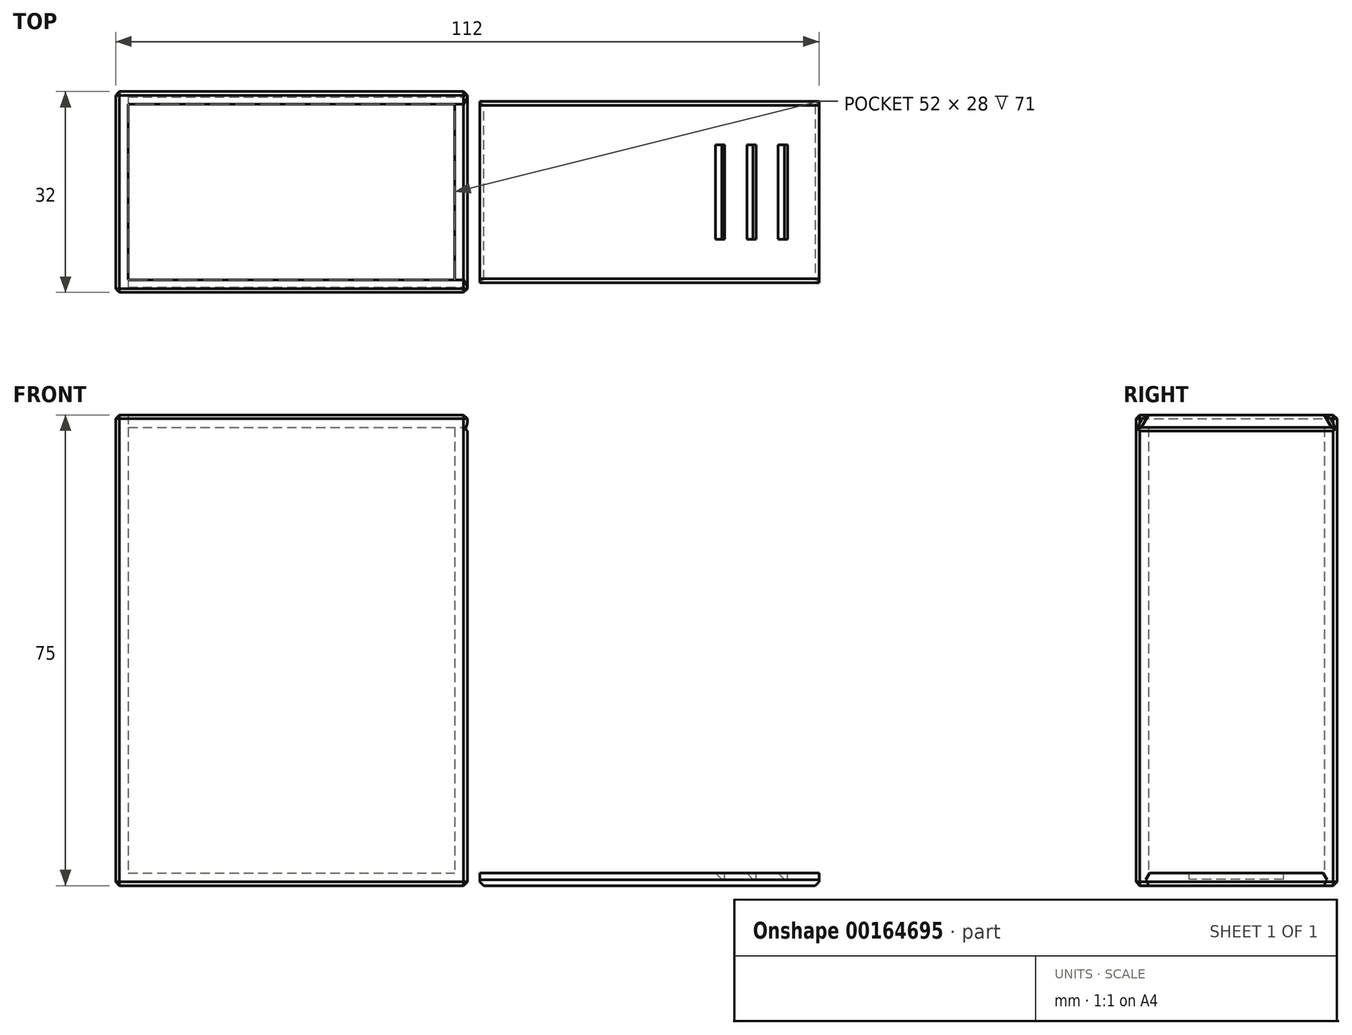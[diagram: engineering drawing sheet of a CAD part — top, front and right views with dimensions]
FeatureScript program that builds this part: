
annotation { "Feature Type Name" : "Feature", "Feature Type Description" : "" }
export const myFeature = defineFeature(function(context is Context, id is Id, definition is map)
    precondition{}
    {
        {
            assignVariable(context, id + "F0", {"name" : "Height", "anyValue" : 75});
        }
        {
            assignVariable(context, id + "F1", {"name" : "Length", "anyValue" : 56});
        }
        {
            assignVariable(context, id + "F2", {"name" : "WallThickness", "anyValue" : 2});
        }
        {
            var Q0;
            Q0=qCreatedBy(makeId("Top.planeOp"),FACE);
            var sketch = newSketch(context, id + "F3", { "sketchPlane" : qUnion([Q0])});
            skLineSegment(sketch, "E0", {"start": v(0, 0) * mm, "end": v(56, 0) * mm});
            skLineSegment(sketch, "E1", {"start": v(56, 0) * mm, "end": v(56, 32) * mm});
            skLineSegment(sketch, "E2", {"start": v(56, 32) * mm, "end": v(0, 32) * mm});
            skLineSegment(sketch, "E3", {"start": v(0, 32) * mm, "end": v(0, 0) * mm});
            skLineSegment(sketch, "E4.0", {"start": v(2, 2) * mm, "end": v(54, 2) * mm});
            skLineSegment(sketch, "E4.1", {"start": v(2, 30) * mm, "end": v(2, 2) * mm});
            skLineSegment(sketch, "E4.2", {"start": v(54, 30) * mm, "end": v(2, 30) * mm});
            skLineSegment(sketch, "E4.3", {"start": v(54, 2) * mm, "end": v(54, 30) * mm});
            skLineSegment(sketch, "E5", {"start": v(54, 2) * mm, "end": v(56, 2) * mm});
            skLineSegment(sketch, "E6", {"start": v(54, 30) * mm, "end": v(56, 30) * mm});
            skLineSegment(sketch, "E7", {"start": v(28, 32) * mm, "end": v(28, 0) * mm, "construction": true});
            skLineSegment(sketch, "E8", {"start": v(29, 2) * mm, "end": v(29, 30) * mm});
            skLineSegment(sketch, "E9.MirrorCS", {"start": v(27, 2) * mm, "end": v(27, 30) * mm});
            skSolve(sketch);
        }
        {
            var Q0;
            Q0=makeQuery(id+"F3.imprint","IMPRINT",FACE,{"disambiguationData":[TD([[makeQuery(id+"F3.imprint","IMPRINT",EDGE,{"derivedFrom":sQuery(id+"F3.wireOp",EDGE,"E0")}),1.0]])]});
            extrude(context, id + "F4", {"entities" : qUnion([Q0]), "depth" : (getVariable(context, 'Height')) * mm});
        }
        {
            var Q0;
            Q0=makeQuery(id+"F3.imprint","IMPRINT",FACE,{"disambiguationData":[TD([[makeQuery(id+"F3.imprint","IMPRINT",EDGE,{"derivedFrom":sQuery(id+"F3.wireOp",EDGE,"E4.0")}),1.0]])]});
            extrude(context, id + "F5", {"entities" : qUnion([Q0]), "operationType" : NewBodyOperationType.ADD, "depth" : (getVariable(context, 'WallThickness')) * mm});
        }
        {
            var Q0;
            Q0=makeQuery(id+"F3.imprint","IMPRINT",FACE,{"disambiguationData":[TD([[makeQuery(id+"F3.imprint","IMPRINT",EDGE,{"derivedFrom":sQuery(id+"F3.wireOp",EDGE,"E4.3")}),-1.0]])]});
            extrude(context, id + "F6", {"entities" : qUnion([Q0]), "operationType" : NewBodyOperationType.ADD, "depth" : (getVariable(context, 'Height') - getVariable(context, 'WallThickness')) * mm});
        }
        {
            var Q0;
            {var subQ0=sQuery(id+"F3.wireOp",EDGE,"E1");Q0=makeQuery(id+"F6.boolean.opBoolean","MERGE",FACE,{"derivedFrom":[makeQuery(id+"F4.opExtrude","SWEPT_FACE",FACE,{"disambiguationData":[OSD([subQ0]),TDD([makeQuery(id+"F3.imprint","IMPRINT",EDGE,{"disambiguationData":[TD([[makeQuery(id+"F3.imprint","INTERSECT",VERTEX,{"derivedFrom":[sQuery(id+"F3.wireOp",EDGE,"E0"),subQ0]}),-1.0]])],"derivedFrom":subQ0})])]}),makeQuery(id+"F4.opExtrude","SWEPT_FACE",FACE,{"disambiguationData":[OSD([subQ0]),TDD([makeQuery(id+"F3.imprint","IMPRINT",EDGE,{"disambiguationData":[TD([[makeQuery(id+"F3.imprint","INTERSECT",VERTEX,{"derivedFrom":[subQ0,sQuery(id+"F3.wireOp",EDGE,"E2")]}),1.0]])],"derivedFrom":subQ0})])]}),makeQuery(id+"F6.opExtrude","SWEPT_FACE",FACE,{"disambiguationData":[OSD([subQ0])]})]});}
            var sketch = newSketch(context, id + "F7", { "sketchPlane" : qUnion([Q0])});
            skLineSegment(sketch, "E10.0", {"start": v(2, 73) * mm, "end": v(30, 73) * mm});
            skLineSegment(sketch, "E10.1", {"start": v(0, 75) * mm, "end": v(2, 75) * mm, "construction": true});
            skLineSegment(sketch, "E10.2", {"start": v(30, 75) * mm, "end": v(32, 75) * mm, "construction": true});
            skLineSegment(sketch, "E10.3", {"start": v(32, 75) * mm, "end": v(32, 0) * mm, "construction": true});
            skLineSegment(sketch, "E10.4", {"start": v(0, 75) * mm, "end": v(0, 0) * mm, "construction": true});
            skLineSegment(sketch, "E11", {"start": v(2, 75) * mm, "end": v(0.85, 73) * mm});
            skLineSegment(sketch, "E12", {"start": v(0.85, 73) * mm, "end": v(2, 73) * mm});
            skPoint(sketch, "E13", {"position": v(16, 73) * mm});
            skLineSegment(sketch, "E14", {"start": v(16, 104.43) * mm, "end": v(16, 92.5) * mm, "construction": true});
            skLineSegment(sketch, "E15.MirrorCS", {"start": v(30, 75) * mm, "end": v(31.15, 73) * mm});
            skLineSegment(sketch, "E16.MirrorCS", {"start": v(31.15, 73) * mm, "end": v(30, 73) * mm});
            skLineSegment(sketch, "E17", {"start": v(2, 75) * mm, "end": v(30, 75) * mm});
            skLineSegment(sketch, "E18", {"start": v(1.05, 73) * mm, "end": v(2.2, 75) * mm});
            skLineSegment(sketch, "E19.MirrorCS", {"start": v(30.95, 73) * mm, "end": v(29.8, 75) * mm});
            skSolve(sketch);
        }
        {
            var Q0;
            Q0=makeQuery(id+"F7.imprint","IMPRINT",FACE,{"disambiguationData":[TD([[makeQuery(id+"F7.imprint","IMPRINT",EDGE,{"derivedFrom":sQuery(id+"F7.wireOp",EDGE,"E11")}),1.0]])]});
            var Q1;
            Q1=makeQuery(id+"F7.imprint","IMPRINT",FACE,{"disambiguationData":[TD([[makeQuery(id+"F7.imprint","IMPRINT",EDGE,{"derivedFrom":sQuery(id+"F7.wireOp",EDGE,"E15.MirrorCS")}),-1.0]])]});
            var Q2;
            {var subQ0=sQuery(id+"F7.wireOp",EDGE,"E12");var subQ3=sQuery(id+"F7.wireOp",EDGE,"E18");var subQ4=makeQuery(id+"F7.imprint","INTERSECT",VERTEX,{"derivedFrom":[subQ0,subQ3]});Q2=makeQuery(id+"F7.imprint","IMPRINT",FACE,{"disambiguationData":[TD([[makeQuery(id+"F7.imprint","IMPRINT",EDGE,{"disambiguationData":[TD([[subQ4,-1.0]])],"derivedFrom":subQ3}),-1.0]])]});}
            var Q3;
            {var subQ0=sQuery(id+"F7.wireOp",EDGE,"E16.MirrorCS");var subQ3=sQuery(id+"F7.wireOp",EDGE,"E19.MirrorCS");var subQ4=makeQuery(id+"F7.imprint","INTERSECT",VERTEX,{"derivedFrom":[subQ0,subQ3]});Q3=makeQuery(id+"F7.imprint","IMPRINT",FACE,{"disambiguationData":[TD([[makeQuery(id+"F7.imprint","IMPRINT",EDGE,{"disambiguationData":[TD([[subQ4,-1.0]])],"derivedFrom":subQ3}),1.0]])]});}
            extrude(context, id + "F8", {"entities" : qUnion([Q0, Q1, Q2, Q3]), "operationType" : NewBodyOperationType.REMOVE, "oppositeDirection" : true, "depth" : (getVariable(context, 'Length') - getVariable(context, 'WallThickness')) * mm});
        }
        {
            var Q0;
            Q0=makeQuery(id+"F7.imprint","IMPRINT",FACE,{"disambiguationData":[TD([[makeQuery(id+"F7.imprint","IMPRINT",EDGE,{"derivedFrom":sQuery(id+"F7.wireOp",EDGE,"E10.0")}),1.0]])]});
            var Q1;
            {var subQ0=sQuery(id+"F7.wireOp",EDGE,"E12");var subQ3=sQuery(id+"F7.wireOp",EDGE,"E18");var subQ4=makeQuery(id+"F7.imprint","INTERSECT",VERTEX,{"derivedFrom":[subQ0,subQ3]});Q1=makeQuery(id+"F7.imprint","IMPRINT",FACE,{"disambiguationData":[TD([[makeQuery(id+"F7.imprint","IMPRINT",EDGE,{"disambiguationData":[TD([[subQ4,-1.0]])],"derivedFrom":subQ3}),-1.0]])]});}
            var Q2;
            {var subQ0=sQuery(id+"F7.wireOp",EDGE,"E16.MirrorCS");var subQ3=sQuery(id+"F7.wireOp",EDGE,"E19.MirrorCS");var subQ4=makeQuery(id+"F7.imprint","INTERSECT",VERTEX,{"derivedFrom":[subQ0,subQ3]});Q2=makeQuery(id+"F7.imprint","IMPRINT",FACE,{"disambiguationData":[TD([[makeQuery(id+"F7.imprint","IMPRINT",EDGE,{"disambiguationData":[TD([[subQ4,-1.0]])],"derivedFrom":subQ3}),1.0]])]});}
            extrude(context, id + "F9", {"entities" : qUnion([Q0, Q1, Q2]), "depth" : (getVariable(context, 'Length')) * mm, "hasSecondDirection" : true, "secondDirectionOppositeDirection" : false, "secondDirectionDepth" : (getVariable(context, 'WallThickness')) * mm});
        }
        {
            var Q0;
            Q0=makeQuery(id+"F9.opExtrude","SWEPT_BODY",BODY,{"disambiguationData":[OSD([sQuery(id+"F7.wireOp",EDGE,"E10.0"),sQuery(id+"F7.wireOp",EDGE,"E12"),sQuery(id+"F7.wireOp",EDGE,"E16.MirrorCS"),sQuery(id+"F7.wireOp",EDGE,"E17"),sQuery(id+"F7.wireOp",EDGE,"E18"),sQuery(id+"F7.wireOp",EDGE,"E19.MirrorCS")])]});
            transform(context, id + "F10", {"entities" : qUnion([Q0]), "transformType" : TransformType.TRANSLATION_3D, "dx" : 0 * mm, "dy" : 0 * mm, "dz" : (-getVariable(context, 'Height') + getVariable(context, 'WallThickness')) * mm, "makeCopy" : false});
        }
        {
            var Q0;
            Q0=makeQuery(id+"F9.opExtrude","SWEPT_FACE",FACE,{"disambiguationData":[OSD([sQuery(id+"F7.wireOp",EDGE,"E17")])]});
            var sketch = newSketch(context, id + "F11", { "sketchPlane" : qUnion([Q0])});
            skLineSegment(sketch, "E20.0", {"start": v(112, 2.2) * mm, "end": v(112, 29.8) * mm, "construction": true});
            skLineSegment(sketch, "E20.1", {"start": v(112, 29.8) * mm, "end": v(58, 29.8) * mm, "construction": true});
            skLineSegment(sketch, "E20.2", {"start": v(112, 2.2) * mm, "end": v(58, 2.2) * mm, "construction": true});
            skLineSegment(sketch, "E20.3", {"start": v(58, 2.2) * mm, "end": v(58, 29.8) * mm, "construction": true});
            skLineSegment(sketch, "E21", {"start": v(107, 23.5) * mm, "end": v(107, 8.5) * mm});
            skLineSegment(sketch, "E22", {"start": v(107, 8.5) * mm, "end": v(104, 8.5) * mm});
            skLineSegment(sketch, "E23", {"start": v(104, 8.5) * mm, "end": v(104, 23.5) * mm});
            skLineSegment(sketch, "E24", {"start": v(104, 23.5) * mm, "end": v(107, 23.5) * mm});
            skPoint(sketch, "E25", {"position": v(107, 16) * mm});
            skPoint(sketch, "E26", {"position": v(112, 16) * mm});
            skLineSegment(sketch, "E27.1.0.0", {"start": v(102, 23.5) * mm, "end": v(102, 8.5) * mm});
            skLineSegment(sketch, "E27.1.0.1", {"start": v(102, 8.5) * mm, "end": v(99, 8.5) * mm});
            skLineSegment(sketch, "E27.1.0.2", {"start": v(99, 8.5) * mm, "end": v(99, 23.5) * mm});
            skLineSegment(sketch, "E27.1.0.3", {"start": v(99, 23.5) * mm, "end": v(102, 23.5) * mm});
            skLineSegment(sketch, "E27.2.0.0", {"start": v(97, 23.5) * mm, "end": v(97, 8.5) * mm});
            skLineSegment(sketch, "E27.2.0.1", {"start": v(97, 8.5) * mm, "end": v(94, 8.5) * mm});
            skLineSegment(sketch, "E27.2.0.2", {"start": v(94, 8.5) * mm, "end": v(94, 23.5) * mm});
            skLineSegment(sketch, "E27.2.0.3", {"start": v(94, 23.5) * mm, "end": v(97, 23.5) * mm});
            skLineSegment(sketch, "E27.direction1", {"start": v(104, 8.5) * mm, "end": v(99, 8.5) * mm, "construction": true});
            skSolve(sketch);
        }
        {
            var Q0;
            Q0=makeQuery(id+"F11.imprint","IMPRINT",FACE,{"disambiguationData":[TD([[makeQuery(id+"F11.imprint","IMPRINT",EDGE,{"derivedFrom":sQuery(id+"F11.wireOp",EDGE,"E27.2.0.0")}),-1.0]])]});
            var Q1;
            Q1=makeQuery(id+"F11.imprint","IMPRINT",FACE,{"disambiguationData":[TD([[makeQuery(id+"F11.imprint","IMPRINT",EDGE,{"derivedFrom":sQuery(id+"F11.wireOp",EDGE,"E27.1.0.0")}),-1.0]])]});
            var Q2;
            Q2=makeQuery(id+"F11.imprint","IMPRINT",FACE,{"disambiguationData":[TD([[makeQuery(id+"F11.imprint","IMPRINT",EDGE,{"derivedFrom":sQuery(id+"F11.wireOp",EDGE,"E21")}),-1.0]])]});
            extrude(context, id + "F12", {"entities" : qUnion([Q0, Q1, Q2]), "operationType" : NewBodyOperationType.REMOVE, "oppositeDirection" : true, "depth" : (getVariable(context, 'WallThickness') / 2) * mm});
        }
        {
            var Q0;
            Q0=makeQuery(id+"F12.boolean.opBoolean","COPY",EDGE,{"derivedFrom":makeQuery(id+"F12.opExtrude","CAP_EDGE",EDGE,{"disambiguationData":[OSD([sQuery(id+"F11.wireOp",EDGE,"E23")])],"isStart":false})});
            var Q1;
            Q1=makeQuery(id+"F12.boolean.opBoolean","COPY",EDGE,{"derivedFrom":makeQuery(id+"F12.opExtrude","CAP_EDGE",EDGE,{"disambiguationData":[OSD([sQuery(id+"F11.wireOp",EDGE,"E27.1.0.2")])],"isStart":false})});
            var Q2;
            Q2=makeQuery(id+"F12.boolean.opBoolean","COPY",EDGE,{"derivedFrom":makeQuery(id+"F12.opExtrude","CAP_EDGE",EDGE,{"disambiguationData":[OSD([sQuery(id+"F11.wireOp",EDGE,"E27.2.0.2")])],"isStart":false})});
            chamfer(context, id + "F13", {"entities" : qUnion([Q0, Q1, Q2]), "width" : 2.5 * mm, "tangentPropagation" : true});
        }
        {
            var Q0;
            Q0=makeQuery(id+"F4.opExtrude","SWEPT_FACE",FACE,{"disambiguationData":[OSD([sQuery(id+"F3.wireOp",EDGE,"E0")])]});
            var sketch = newSketch(context, id + "F14", { "sketchPlane" : qUnion([Q0])});
            skLineSegment(sketch, "E28.0", {"start": v(0, 75) * mm, "end": v(0, 0) * mm, "construction": true});
            skLineSegment(sketch, "E28.1", {"start": v(0, 75) * mm, "end": v(56, 75) * mm, "construction": true});
            skLineSegment(sketch, "E28.2", {"start": v(56, 75) * mm, "end": v(56, 0) * mm, "construction": true});
            skLineSegment(sketch, "E28.3", {"start": v(0, 0) * mm, "end": v(56, 0) * mm, "construction": true});
            skLineSegment(sketch, "E29", {"start": v(0, 37.5) * mm, "end": v(56, 37.5) * mm, "construction": true});
            skLineSegment(sketch, "E30", {"start": v(28, 75) * mm, "end": v(28, 0) * mm, "construction": true});
            skLineSegment(sketch, "E31", {"start": v(28, 55.5) * mm, "end": v(22, 55.5) * mm});
            skLineSegment(sketch, "E32", {"start": v(22, 55.5) * mm, "end": v(22, 43.5) * mm});
            skLineSegment(sketch, "E33", {"start": v(22, 43.5) * mm, "end": v(10, 43.5) * mm});
            skLineSegment(sketch, "E34", {"start": v(10, 43.5) * mm, "end": v(10, 37.5) * mm});
            skLineSegment(sketch, "E35.MirrorCS", {"start": v(28, 55.5) * mm, "end": v(34, 55.5) * mm});
            skLineSegment(sketch, "E36.MirrorCS", {"start": v(34, 55.5) * mm, "end": v(34, 43.5) * mm});
            skLineSegment(sketch, "E37.MirrorCS", {"start": v(46, 43.5) * mm, "end": v(46, 37.5) * mm});
            skLineSegment(sketch, "E38.MirrorCS", {"start": v(34, 43.5) * mm, "end": v(46, 43.5) * mm});
            skLineSegment(sketch, "E39.MirrorCS", {"start": v(10, 31.5) * mm, "end": v(10, 37.5) * mm});
            skLineSegment(sketch, "E40.MirrorCS", {"start": v(22, 31.5) * mm, "end": v(10, 31.5) * mm});
            skLineSegment(sketch, "E41.MirrorCS", {"start": v(22, 19.5) * mm, "end": v(22, 31.5) * mm});
            skLineSegment(sketch, "E42.MirrorCS", {"start": v(28, 19.5) * mm, "end": v(22, 19.5) * mm});
            skLineSegment(sketch, "E43.MirrorCS", {"start": v(28, 19.5) * mm, "end": v(34, 19.5) * mm});
            skLineSegment(sketch, "E44.MirrorCS", {"start": v(34, 19.5) * mm, "end": v(34, 31.5) * mm});
            skLineSegment(sketch, "E45.MirrorCS", {"start": v(46, 31.5) * mm, "end": v(46, 37.5) * mm});
            skLineSegment(sketch, "E46.MirrorCS", {"start": v(34, 31.5) * mm, "end": v(46, 31.5) * mm});
            skSolve(sketch);
        }
        {
            var Q0;
            Q0=makeQuery(id+"F4.opExtrude","SWEPT_FACE",FACE,{"disambiguationData":[OSD([sQuery(id+"F3.wireOp",EDGE,"E0")])]});
            var Q1;
            {var subQ0=sQuery(id+"F3.wireOp",EDGE,"E1");Q1=makeQuery(id+"F6.boolean.opBoolean","MERGE",FACE,{"derivedFrom":[makeQuery(id+"F4.opExtrude","SWEPT_FACE",FACE,{"disambiguationData":[OSD([subQ0]),TDD([makeQuery(id+"F3.imprint","IMPRINT",EDGE,{"disambiguationData":[TD([[makeQuery(id+"F3.imprint","INTERSECT",VERTEX,{"derivedFrom":[sQuery(id+"F3.wireOp",EDGE,"E0"),subQ0]}),-1.0]])],"derivedFrom":subQ0})])]}),makeQuery(id+"F4.opExtrude","SWEPT_FACE",FACE,{"disambiguationData":[OSD([subQ0]),TDD([makeQuery(id+"F3.imprint","IMPRINT",EDGE,{"disambiguationData":[TD([[makeQuery(id+"F3.imprint","INTERSECT",VERTEX,{"derivedFrom":[subQ0,sQuery(id+"F3.wireOp",EDGE,"E2")]}),1.0]])],"derivedFrom":subQ0})])]}),makeQuery(id+"F6.opExtrude","SWEPT_FACE",FACE,{"disambiguationData":[OSD([subQ0])]})]});}
            var Q2;
            Q2=makeQuery(id+"F4.opExtrude","SWEPT_FACE",FACE,{"disambiguationData":[OSD([sQuery(id+"F3.wireOp",EDGE,"E2")])]});
            var Q3;
            Q3=makeQuery(id+"F4.opExtrude","SWEPT_FACE",FACE,{"disambiguationData":[OSD([sQuery(id+"F3.wireOp",EDGE,"E3")])]});
            var Q4;
            {var subQ0=sQuery(id+"F3.wireOp",EDGE,"E6");var subQ1=sQuery(id+"F3.wireOp",EDGE,"E5");var subQ2=sQuery(id+"F3.wireOp",EDGE,"E4.3");var subQ3=sQuery(id+"F3.wireOp",EDGE,"E1");var subQ4=sQuery(id+"F3.wireOp",EDGE,"E4.2");var subQ5=sQuery(id+"F3.wireOp",EDGE,"E4.1");var subQ6=sQuery(id+"F3.wireOp",EDGE,"E4.0");Q4=makeQuery(id+"F6.boolean.opBoolean","MERGE",FACE,{"derivedFrom":[makeQuery(id+"F5.boolean.opBoolean","MERGE",FACE,{"derivedFrom":[makeQuery(id+"F4.opExtrude","CAP_FACE",FACE,{"disambiguationData":[OSD([sQuery(id+"F3.wireOp",EDGE,"E0"),subQ3,sQuery(id+"F3.wireOp",EDGE,"E2"),sQuery(id+"F3.wireOp",EDGE,"E3"),subQ6,subQ5,subQ4,subQ1,subQ0])],"isStart":true}),makeQuery(id+"F5.opExtrude","CAP_FACE",FACE,{"disambiguationData":[OSD([subQ6,subQ5,subQ4,subQ2])],"isStart":true})]}),makeQuery(id+"F6.opExtrude","CAP_FACE",FACE,{"disambiguationData":[OSD([subQ3,subQ2,subQ1,subQ0])],"isStart":true})]});}
            var Q5;
            Q5=makeQuery(id+"F9.opExtrude","SWEPT_FACE",FACE,{"disambiguationData":[OSD([sQuery(id+"F7.wireOp",EDGE,"E10.0"),sQuery(id+"F7.wireOp",EDGE,"E12"),sQuery(id+"F7.wireOp",EDGE,"E16.MirrorCS")])]});
            chamfer(context, id + "F15", {"entities" : qUnion([Q0, Q1, Q2, Q3, Q4, Q5]), "width" : 0.6 * mm, "tangentPropagation" : true});
        }
    });
